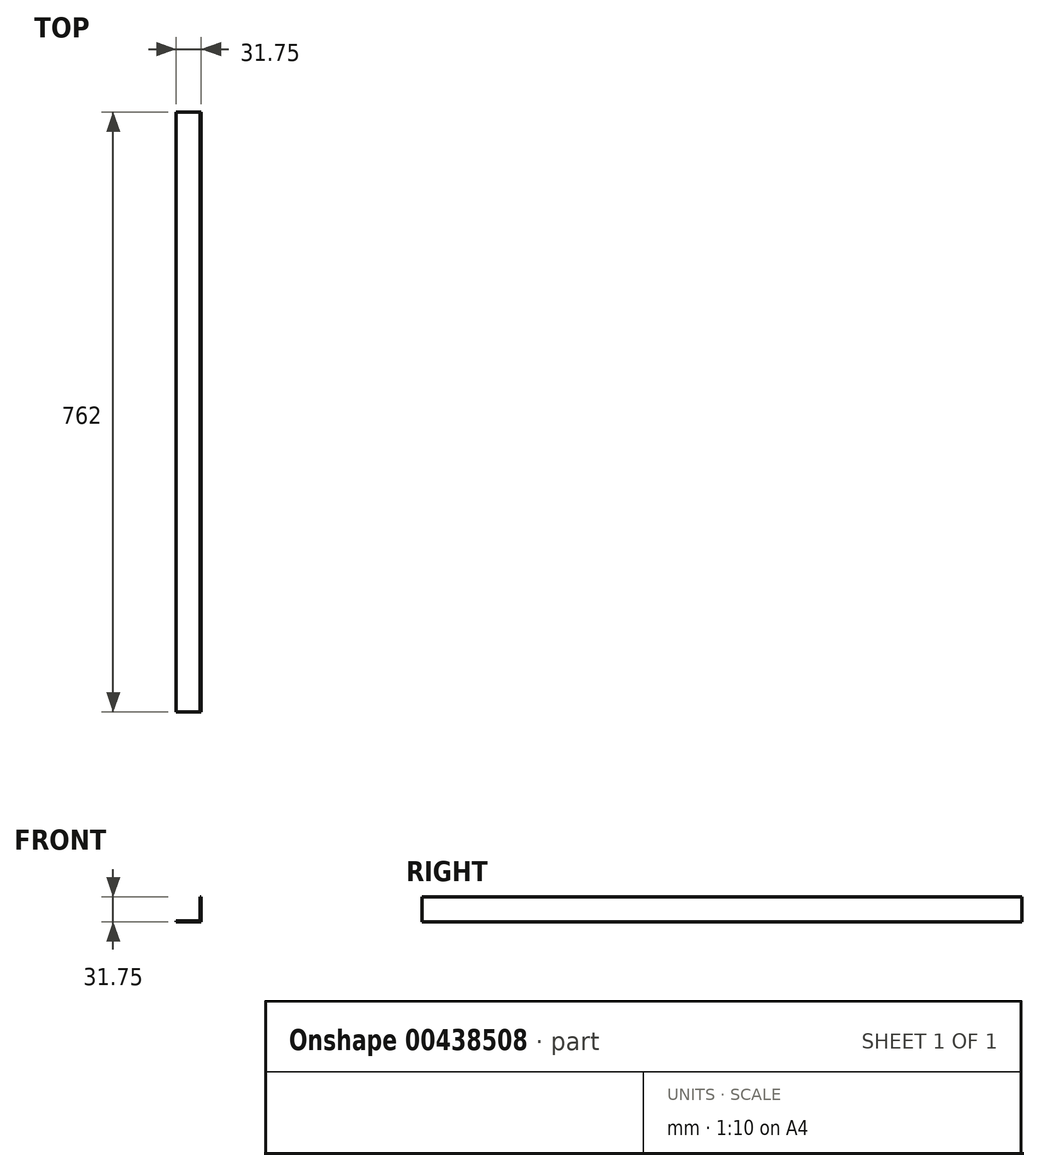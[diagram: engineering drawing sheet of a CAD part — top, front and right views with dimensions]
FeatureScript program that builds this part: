
annotation { "Feature Type Name" : "Feature", "Feature Type Description" : "" }
export const myFeature = defineFeature(function(context is Context, id is Id, definition is map)
    precondition{}
    {
        {
            var Q0;
            Q0=qCreatedBy(makeId("Front.planeOp"),FACE);
            var sketch = newSketch(context, id + "F0", { "sketchPlane" : qUnion([Q0])});
            skLineSegment(sketch, "E0", {"start": v(0, 0) * mm, "end": v(0, 31.75) * mm});
            skLineSegment(sketch, "E1", {"start": v(0, 31.75) * mm, "end": v(-1.2, 31.75) * mm});
            skLineSegment(sketch, "E2", {"start": v(-1.2, 31.75) * mm, "end": v(-1.2, 1.2) * mm});
            skLineSegment(sketch, "E3", {"start": v(-1.2, 1.2) * mm, "end": v(-31.75, 1.2) * mm});
            skLineSegment(sketch, "E4", {"start": v(-31.75, 1.2) * mm, "end": v(-31.75, 0) * mm});
            skLineSegment(sketch, "E5", {"start": v(-31.75, 0) * mm, "end": v(0, 0) * mm});
            skSolve(sketch);
        }
        {
            var Q0;
            Q0 = qSketchRegion(id + "F0", true);
            extrude(context, id + "F1", {"entities" : qUnion([Q0]), "depth" : 762 * mm});
        }
    });
